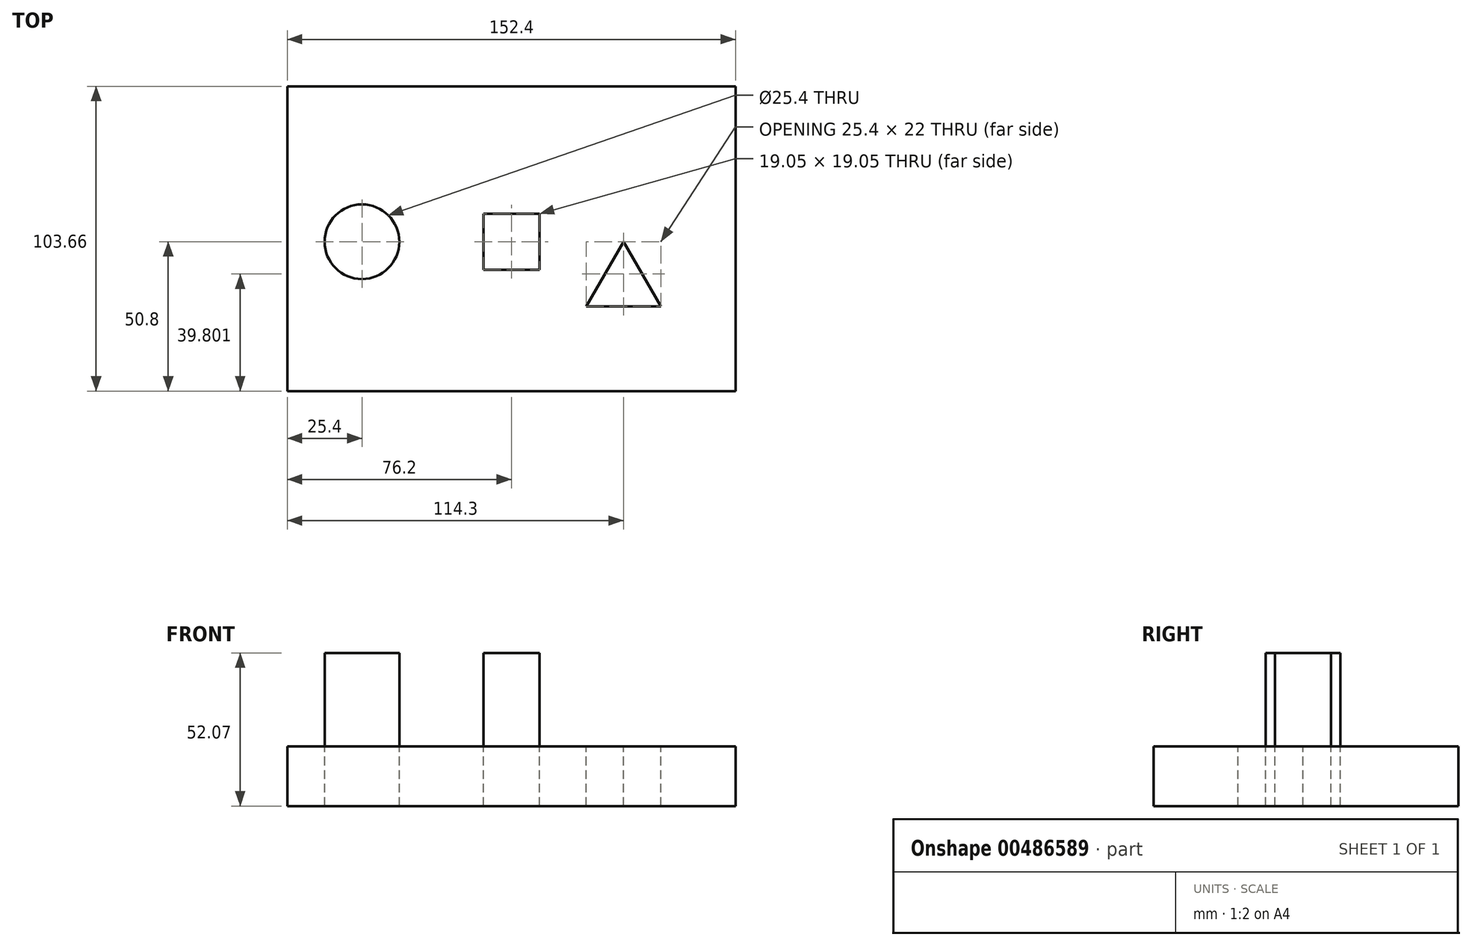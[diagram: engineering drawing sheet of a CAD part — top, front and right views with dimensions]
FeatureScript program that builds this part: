
annotation { "Feature Type Name" : "Feature", "Feature Type Description" : "" }
export const myFeature = defineFeature(function(context is Context, id is Id, definition is map)
    precondition{}
    {
        {
            var Q0;
            Q0=qCreatedBy(makeId("Top.planeOp"),FACE);
            var sketch = newSketch(context, id + "F0", { "sketchPlane" : qUnion([Q0])});
            skPoint(sketch, "E0.middle", {"position": v(0, 0) * mm});
            skLineSegment(sketch, "E1.bottom", {"start": v(-107.95, 52.86) * mm, "end": v(44.45, 52.86) * mm});
            skLineSegment(sketch, "E1.top", {"start": v(-107.95, -50.8) * mm, "end": v(44.45, -50.8) * mm});
            skLineSegment(sketch, "E1.left", {"start": v(-107.95, 52.86) * mm, "end": v(-107.95, -50.8) * mm});
            skLineSegment(sketch, "E1.right", {"start": v(44.45, 52.86) * mm, "end": v(44.45, -50.8) * mm});
            skCircle(sketch, "E2.cCircle", {"center": v(6.35, -14.66) * mm, "radius": 14.66 * mm, "construction": true});
            skLineSegment(sketch, "E2.0", {"start": v(6.35, 0) * mm, "end": v(19.05, -22) * mm});
            skLineSegment(sketch, "E2.1", {"start": v(19.05, -22) * mm, "end": v(-6.35, -22) * mm});
            skLineSegment(sketch, "E2.2", {"start": v(-6.35, -22) * mm, "end": v(6.35, 0) * mm});
            skLineSegment(sketch, "E3.bottom", {"start": v(-41.28, 9.52) * mm, "end": v(-22.22, 9.52) * mm});
            skLineSegment(sketch, "E3.top", {"start": v(-41.28, -9.52) * mm, "end": v(-22.23, -9.52) * mm});
            skLineSegment(sketch, "E3.left", {"start": v(-41.28, 9.53) * mm, "end": v(-41.28, -9.53) * mm});
            skLineSegment(sketch, "E3.right", {"start": v(-22.22, 9.53) * mm, "end": v(-22.23, -9.53) * mm});
            skPoint(sketch, "E3.middle", {"position": v(-31.75, 0) * mm});
            skCircle(sketch, "E4", {"center": v(-82.55, 0) * mm, "radius": 12.7 * mm});
            skSolve(sketch);
        }
        {
            var Q0;
            Q0=makeQuery(id+"F0.imprint","IMPRINT",FACE,{"disambiguationData":[TD([[makeQuery(id+"F0.imprint","IMPRINT",EDGE,{"derivedFrom":sQuery(id+"F0.wireOp",EDGE,"E4")}),1.0]])]});
            var Q1;
            Q1=makeQuery(id+"F0.imprint","IMPRINT",FACE,{"disambiguationData":[TD([[makeQuery(id+"F0.imprint","IMPRINT",EDGE,{"derivedFrom":sQuery(id+"F0.wireOp",EDGE,"E3.bottom")}),-1.0]])]});
            extrude(context, id + "F1", {"entities" : qUnion([Q0, Q1]), "depth" : 31.75 * mm});
        }
        {
            var Q0;
            Q0=makeQuery(id+"F0.imprint","IMPRINT",FACE,{"disambiguationData":[TD([[makeQuery(id+"F0.imprint","IMPRINT",EDGE,{"derivedFrom":sQuery(id+"F0.wireOp",EDGE,"E1.bottom")}),-1.0]])]});
            extrude(context, id + "F2", {"entities" : qUnion([Q0]), "oppositeDirection" : true, "depth" : 20.32 * mm});
        }
        {
            var Q0;
            Q0=makeQuery(id+"F0.imprint","IMPRINT",FACE,{"disambiguationData":[TD([[makeQuery(id+"F0.imprint","IMPRINT",EDGE,{"derivedFrom":sQuery(id+"F0.wireOp",EDGE,"E4")}),1.0]])]});
            var Q1;
            Q1=makeQuery(id+"F0.imprint","IMPRINT",FACE,{"disambiguationData":[TD([[makeQuery(id+"F0.imprint","IMPRINT",EDGE,{"derivedFrom":sQuery(id+"F0.wireOp",EDGE,"E3.bottom")}),-1.0]])]});
            extrude(context, id + "F3", {"entities" : qUnion([Q0, Q1]), "oppositeDirection" : true, "depth" : 20.32 * mm});
        }
    });
